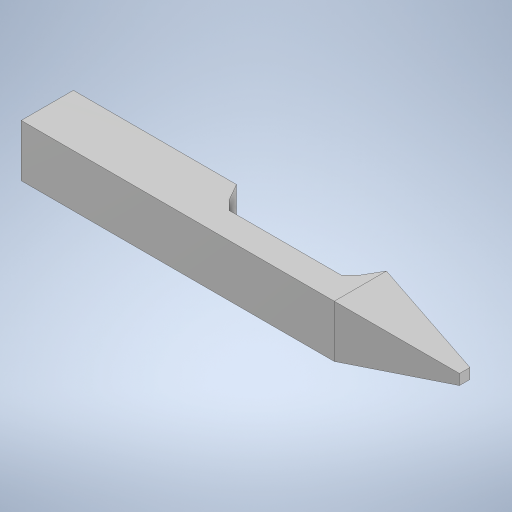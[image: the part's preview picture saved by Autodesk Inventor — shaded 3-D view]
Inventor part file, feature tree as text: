
AUTODESK INVENTOR PART (.ipt)
format: ipt  version: 2023 (Build 270158030, 158C)  size: 398,336 bytes
history: mixed  units: in
note: dims shown in document units (in); Inventor stores cm internally (conversion verified against a paired STEP export)
features: other x6, extrude x2, sketch x2, move_body x2, direct_edit x1, imported_body x1
ambient origin geometry x8: Origin, YZ Plane, XZ Plane, XY Plane, X Axis, Y Axis, Z Axis, Center Point
bodies: Solid1 (imported_parasolid), Solid4 (imported_parasolid), Solid6 (imported_parasolid), Solid10 (imported_parasolid), Solid23 (imported_parasolid), Solid37 (imported_parasolid)
feature tree (14):
  other  "MouseEarbar"
  extrude  "Extrusion1"  TaperAngle=120.0deg  [1 undecoded]
  extrude  "Extrusion2"  TaperAngle=120.0deg  [1 undecoded]
  direct_edit  "Direct Edit1"
  sketch  "Sketch1"  dims[d0=0.0591in d1=120.0deg]
  sketch  "Sketch2"  dims[d2=0.3937in d3=120.0deg d4=0.0591in d5=0.0in d6=0.0in d7=0.0394in d8=135.0deg d9=0.0394in d10=0.0in d11=0.0in d12=0.0in d13=0.0in d14=1.1811in d15=0.0in d16=0.0in d17=0.0787in]
  other  "Rat_ToothHolder"
  other  "Mouse_ToothHolder"
  other  "MouseNoseCone"
  other  "RatNoseCone"
  other  "RatEarbar_1"
  move_body  "Move1"
  move_body  "Move2"
  imported_body  NMx_Import_Brep_tag  [imported B-rep: ~21 faces, bbox_mm=[32.0, 4.0, 4.0]]
note: 2 required parameter values undecoded (feature->parameter linkage not recoverable at this tier; creation-order binding heuristic only, values carry confidence <= 0.55)
